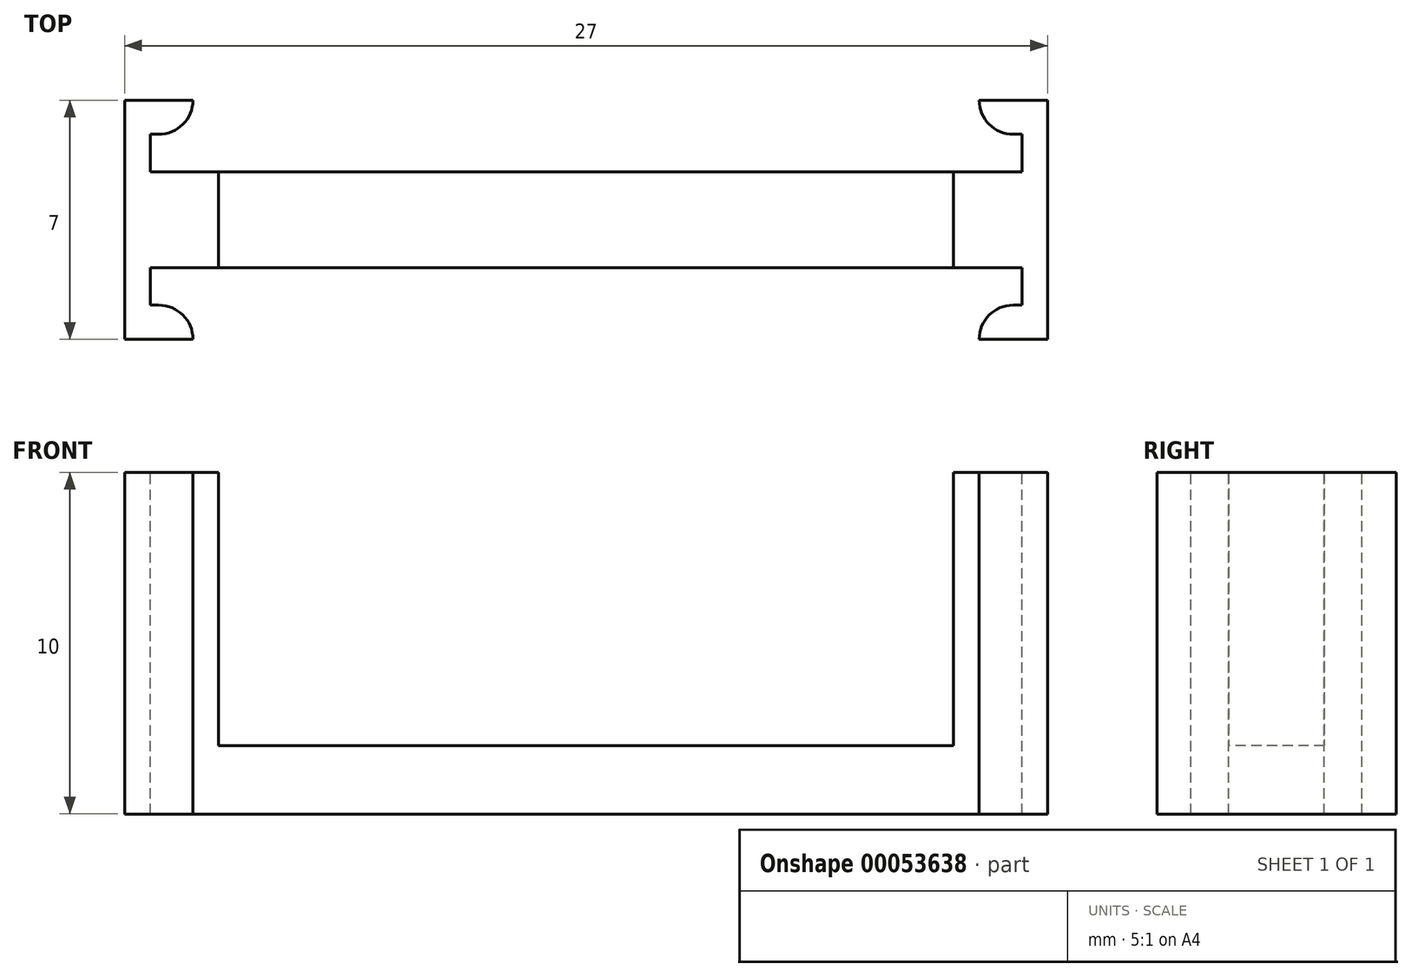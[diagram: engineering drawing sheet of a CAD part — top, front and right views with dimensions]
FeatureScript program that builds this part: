
annotation { "Feature Type Name" : "Feature", "Feature Type Description" : "" }
export const myFeature = defineFeature(function(context is Context, id is Id, definition is map)
    precondition{}
    {
        {
            var Q0;
            Q0=qCreatedBy(makeId("Front.planeOp"),FACE);
            var sketch = newSketch(context, id + "F0", { "sketchPlane" : qUnion([Q0])});
            skArc(sketch, "E0", {"start": v(0, 4.09) * mm, "mid": v(0.48, 4.1) * mm, "end": v(0.97, 4.15) * mm});
            skLineSegment(sketch, "E1", {"start": v(3.5, 7.49) * mm, "end": v(10.06, -2.83) * mm});
            skLineSegment(sketch, "E2", {"start": v(10.06, -2.83) * mm, "end": v(10.06, -5.91) * mm});
            skLineSegment(sketch, "E3", {"start": v(10.06, -5.91) * mm, "end": v(7.8, -5.91) * mm});
            skArc(sketch, "E4", {"start": v(7.8, -5.91) * mm, "mid": v(6.65, 0.66) * mm, "end": v(0.97, 4.15) * mm});
            skPoint(sketch, "E5.orphan", {"position": v(0, -5.91) * mm});
            skLineSegment(sketch, "E6", {"start": v(0, 4.09) * mm, "end": v(0, -5.91) * mm, "construction": true});
            skLineSegment(sketch, "E7", {"start": v(0, 4.09) * mm, "end": v(0, 7.49) * mm});
            skLineSegment(sketch, "E8", {"start": v(0, 7.49) * mm, "end": v(0, 9.49) * mm});
            skLineSegment(sketch, "E9", {"start": v(0, 9.49) * mm, "end": v(3.5, 9.49) * mm});
            skLineSegment(sketch, "E10", {"start": v(3.5, 9.49) * mm, "end": v(3.5, 7.49) * mm});
            skSolve(sketch);
        }
        {
            var Q0;
            Q0=qSketchRegion(id+"F0",true);
            var Q1;
            Q1=sQuery(id+"F0.wireOp",EDGE,"E6");
            revolve(context, id + "F1", {"entities" : qUnion([Q0]), "axis" : qUnion([Q1]), "revolveType" : RevolveType.FULL});
        }
        {
            var Q0;
            Q0=qCreatedBy(makeId("Top.planeOp"),FACE);
            var sketch = newSketch(context, id + "F2", { "sketchPlane" : qUnion([Q0])});
            skCircle(sketch, "E11", {"center": v(0, 0) * mm, "radius": 3 * mm});
            skSolve(sketch);
        }
        {
            var Q0;
            Q0=qSketchRegion(id+"F2",true);
            extrude(context, id + "F3", {"entities" : qUnion([Q0]), "operationType" : NewBodyOperationType.REMOVE, "endBound" : BoundingType.SYMMETRIC, "oppositeDirection" : true, "depth" : 50 * mm});
        }
        {
            var Q0;
            Q0=qCreatedBy(makeId("Right.planeOp"),FACE);
            var sketch = newSketch(context, id + "F4", { "sketchPlane" : qUnion([Q0])});
            skLineSegment(sketch, "E12.bottom", {"start": v(1, -5.91) * mm, "end": v(-1, -5.91) * mm});
            skLineSegment(sketch, "E12.left", {"start": v(1, -5.91) * mm, "end": v(1, -0.91) * mm});
            skLineSegment(sketch, "E12.right", {"start": v(-1, -5.91) * mm, "end": v(-1, -0.91) * mm});
            skArc(sketch, "E13", {"start": v(1, -0.91) * mm, "mid": v(0, 0.09) * mm, "end": v(-1, -0.91) * mm});
            skSolve(sketch);
        }
        {
            var Q0;
            Q0=qSketchRegion(id+"F4",true);
            extrude(context, id + "F5", {"entities" : qUnion([Q0]), "operationType" : NewBodyOperationType.REMOVE, "endBound" : BoundingType.SYMMETRIC, "oppositeDirection" : true, "depth" : 25 * mm});
        }
        {
            var Q0;
            Q0=makeQuery(id+"F1.opRevolve","SWEPT_EDGE",EDGE,{"disambiguationData":[OSD([sQuery(id+"F0.wireOp",EDGE,"E9"),sQuery(id+"F0.wireOp",EDGE,"E10")])]});
            fillet(context, id + "F6", {"entities" : qUnion([Q0]), "radius" : 1 * mm, "tangentPropagation" : true, "allowEdgeOverflow" : false});
        }
        {
            var Q0;
            {var subQ0=sQuery(id+"F0.wireOp",EDGE,"E2");var subQ1=sQuery(id+"F0.wireOp",EDGE,"E3");Q0=makeQuery(id+"F5.boolean.opBoolean","SPLIT",EDGE,{"disambiguationData":[TD([makeQuery(id+"F5.opExtrude","SWEPT_FACE",FACE,{"disambiguationData":[OSD([sQuery(id+"F4.wireOp",EDGE,"E12.right")])]})])],"derivedFrom":makeQuery(id+"F1.opRevolve","SWEPT_EDGE",EDGE,{"disambiguationData":[OSD([subQ0,subQ1])]})});}
            var Q1;
            {var subQ0=sQuery(id+"F0.wireOp",EDGE,"E2");var subQ1=sQuery(id+"F0.wireOp",EDGE,"E3");Q1=makeQuery(id+"F5.boolean.opBoolean","SPLIT",EDGE,{"disambiguationData":[TD([makeQuery(id+"F5.opExtrude","SWEPT_FACE",FACE,{"disambiguationData":[OSD([sQuery(id+"F4.wireOp",EDGE,"E12.left")])]})])],"derivedFrom":makeQuery(id+"F1.opRevolve","SWEPT_EDGE",EDGE,{"disambiguationData":[OSD([subQ0,subQ1])]})});}
            fillet(context, id + "F7", {"entities" : qUnion([Q0, Q1]), "radius" : 1 * mm, "tangentPropagation" : true, "allowEdgeOverflow" : false});
        }
        {
            var Q0;
            Q0=qCreatedBy(makeId("Front.planeOp"),FACE);
            var sketch = newSketch(context, id + "F8", { "sketchPlane" : qUnion([Q0])});
            skLineSegment(sketch, "E14.bottom", {"start": v(-13.5, 17.49) * mm, "end": v(13.5, 17.49) * mm});
            skLineSegment(sketch, "E14.top", {"start": v(-13.5, 7.49) * mm, "end": v(13.5, 7.49) * mm});
            skLineSegment(sketch, "E14.left", {"start": v(-13.5, 17.49) * mm, "end": v(-13.5, 7.49) * mm});
            skLineSegment(sketch, "E14.right", {"start": v(13.5, 17.49) * mm, "end": v(13.5, 7.49) * mm});
            skSolve(sketch);
        }
        {
            var Q0;
            Q0=qSketchRegion(id+"F8",true);
            extrude(context, id + "F9", {"entities" : qUnion([Q0]), "operationType" : NewBodyOperationType.ADD, "endBound" : BoundingType.SYMMETRIC, "depth" : 7 * mm, "offsetDistance" : 25 * mm});
        }
        {
            var Q0;
            Q0=makeQuery(id+"F9.opExtrude","SWEPT_FACE",FACE,{"disambiguationData":[OSD([sQuery(id+"F8.wireOp",EDGE,"E14.bottom")])]});
            var sketch = newSketch(context, id + "F10", { "sketchPlane" : qUnion([Q0])});
            skLineSegment(sketch, "E15.bottom", {"start": v(-12.75, 2.5) * mm, "end": v(-11.5, 2.5) * mm});
            skLineSegment(sketch, "E15.top", {"start": v(-12.75, 1.4) * mm, "end": v(12.75, 1.4) * mm});
            skLineSegment(sketch, "E15.left", {"start": v(-12.75, 2.5) * mm, "end": v(-12.75, 1.4) * mm});
            skLineSegment(sketch, "E15.right", {"start": v(12.75, 2.5) * mm, "end": v(12.75, 1.4) * mm});
            skLineSegment(sketch, "E16", {"start": v(-11.5, 2.5) * mm, "end": v(-11.5, 3.5) * mm});
            skLineSegment(sketch, "E17", {"start": v(-11.5, 3.5) * mm, "end": v(11.5, 3.5) * mm});
            skLineSegment(sketch, "E18", {"start": v(11.5, 3.5) * mm, "end": v(11.5, 2.5) * mm});
            skLineSegment(sketch, "E19.trimOffspring", {"start": v(11.5, 2.5) * mm, "end": v(12.75, 2.5) * mm});
            skLineSegment(sketch, "E20.MirrorCS", {"start": v(-11.5, -3.5) * mm, "end": v(11.5, -3.5) * mm});
            skLineSegment(sketch, "E21.MirrorCS", {"start": v(-12.75, -1.4) * mm, "end": v(12.75, -1.4) * mm});
            skLineSegment(sketch, "E22.MirrorCS", {"start": v(12.75, -2.5) * mm, "end": v(12.75, -1.4) * mm});
            skLineSegment(sketch, "E23.MirrorCS", {"start": v(11.5, -2.5) * mm, "end": v(12.75, -2.5) * mm});
            skLineSegment(sketch, "E24.MirrorCS", {"start": v(11.5, -3.5) * mm, "end": v(11.5, -2.5) * mm});
            skLineSegment(sketch, "E25.MirrorCS", {"start": v(-11.5, -2.5) * mm, "end": v(-11.5, -3.5) * mm});
            skLineSegment(sketch, "E26.MirrorCS", {"start": v(-12.75, -2.5) * mm, "end": v(-11.5, -2.5) * mm});
            skLineSegment(sketch, "E27.MirrorCS", {"start": v(-12.75, -2.5) * mm, "end": v(-12.75, -1.4) * mm});
            skSolve(sketch);
        }
        {
            var Q0;
            Q0=qSketchRegion(id+"F10",true);
            var Q1;
            {var subQ0=sQuery(id+"F8.wireOp",EDGE,"E14.right");var subQ2=sQuery(id+"F8.wireOp",EDGE,"E14.top");var subQ4=makeQuery(id+"F9.opExtrude","SWEPT_FACE",FACE,{"disambiguationData":[OSD([subQ2])]});Q1=makeQuery(id+"F9.boolean.opBoolean","SPLIT",FACE,{"disambiguationData":[TD([makeQuery(id+"F9.opExtrude","SWEPT_FACE",FACE,{"disambiguationData":[OSD([subQ0])]})])],"derivedFrom":subQ4});}
            extrude(context, id + "F11", {"entities" : qUnion([Q0]), "operationType" : NewBodyOperationType.REMOVE, "endBound" : BoundingType.UP_TO_SURFACE, "oppositeDirection" : true, "depth" : 25 * mm, "endBoundEntityFace" : qUnion([Q1]), "offsetDistance" : 25 * mm});
        }
        {
            var Q0;
            Q0=makeQuery(id+"F9.boolean.opBoolean","SPLIT",FACE,{"disambiguationData":[TD([makeQuery(id+"F3.boolean.opBoolean","COPY",FACE,{"derivedFrom":makeQuery(id+"F3.opExtrude","SWEPT_FACE",FACE,{"disambiguationData":[OSD([sQuery(id+"F2.wireOp",EDGE,"E11")])]})})])],"derivedFrom":makeQuery(id+"F9.opExtrude","SWEPT_FACE",FACE,{"disambiguationData":[OSD([sQuery(id+"F8.wireOp",EDGE,"E14.top")])]})});
            var sketch = newSketch(context, id + "F12", { "sketchPlane" : qUnion([Q0])});
            skCircle(sketch, "E28", {"center": v(0, 0) * mm, "radius": 3.07 * mm});
            skSolve(sketch);
        }
        {
            var Q0;
            Q0=qSketchRegion(id+"F12",true);
            extrude(context, id + "F13", {"entities" : qUnion([Q0]), "operationType" : NewBodyOperationType.ADD, "depth" : 2 * mm, "offsetDistance" : 25 * mm});
        }
        {
            var Q0;
            {var subQ0=sQuery(id+"F10.wireOp",EDGE,"E21.MirrorCS");var subQ1=makeQuery(id+"F11.opExtrude","SWEPT_FACE",FACE,{"disambiguationData":[OSD([subQ0])]});var subQ2=makeQuery(id+"F11.opExtrude","CAP_FACE",FACE,{"disambiguationData":[OSD([subQ0,sQuery(id+"F10.wireOp",EDGE,"E22.MirrorCS"),sQuery(id+"F10.wireOp",EDGE,"E23.MirrorCS"),sQuery(id+"F10.wireOp",EDGE,"E24.MirrorCS"),sQuery(id+"F10.wireOp",EDGE,"E25.MirrorCS"),sQuery(id+"F10.wireOp",EDGE,"E26.MirrorCS"),sQuery(id+"F10.wireOp",EDGE,"E27.MirrorCS"),sQuery(id+"F10.wireOp",EDGE,"E20.MirrorCS")])],"isStart":false});var subQ3=makeQuery(id+"F11.opExtrude","CAP_EDGE",EDGE,{"disambiguationData":[OSD([subQ0])],"isStart":false});var subQ4=makeQuery(id+"F9.opExtrude","SWEPT_FACE",FACE,{"disambiguationData":[OSD([sQuery(id+"F8.wireOp",EDGE,"E14.top")])]});Q0=makeQuery(id+"F13.boolean.opBoolean","MERGE",EDGE,{"derivedFrom":[makeQuery(id+"F11.boolean.opBoolean","COPY",EDGE,{"disambiguationData":[topologyDisambiguationEdgeConnected([subQ4,subQ1]),TD([makeQuery(id+"F3.boolean.opBoolean","COPY",FACE,{"derivedFrom":makeQuery(id+"F3.opExtrude","SWEPT_FACE",FACE,{"disambiguationData":[OSD([sQuery(id+"F2.wireOp",EDGE,"E11")])]})})])],"derivedFrom":subQ3}),makeQuery(id+"F11.boolean.opBoolean","COPY",EDGE,{"disambiguationData":[topologyDisambiguationEdgeConnected([subQ1,subQ2]),OD(0.0)],"derivedFrom":subQ3}),makeQuery(id+"F11.boolean.opBoolean","COPY",EDGE,{"disambiguationData":[topologyDisambiguationEdgeConnected([subQ1,subQ2]),OD(1.0)],"derivedFrom":subQ3})]});}
            var Q1;
            {var subQ0=sQuery(id+"F10.wireOp",EDGE,"E15.top");var subQ1=makeQuery(id+"F11.opExtrude","CAP_FACE",FACE,{"disambiguationData":[OSD([sQuery(id+"F10.wireOp",EDGE,"E15.bottom"),subQ0,sQuery(id+"F10.wireOp",EDGE,"E15.left"),sQuery(id+"F10.wireOp",EDGE,"E15.right"),sQuery(id+"F10.wireOp",EDGE,"E16"),sQuery(id+"F10.wireOp",EDGE,"E17"),sQuery(id+"F10.wireOp",EDGE,"E18"),sQuery(id+"F10.wireOp",EDGE,"E19.trimOffspring")])],"isStart":false});var subQ2=makeQuery(id+"F11.opExtrude","SWEPT_FACE",FACE,{"disambiguationData":[OSD([subQ0])]});var subQ3=makeQuery(id+"F11.opExtrude","CAP_EDGE",EDGE,{"disambiguationData":[OSD([subQ0])],"isStart":false});var subQ4=makeQuery(id+"F9.opExtrude","SWEPT_FACE",FACE,{"disambiguationData":[OSD([sQuery(id+"F8.wireOp",EDGE,"E14.top")])]});Q1=makeQuery(id+"F13.boolean.opBoolean","MERGE",EDGE,{"derivedFrom":[makeQuery(id+"F11.boolean.opBoolean","COPY",EDGE,{"disambiguationData":[topologyDisambiguationEdgeConnected([subQ4,subQ2]),TD([makeQuery(id+"F3.boolean.opBoolean","COPY",FACE,{"derivedFrom":makeQuery(id+"F3.opExtrude","SWEPT_FACE",FACE,{"disambiguationData":[OSD([sQuery(id+"F2.wireOp",EDGE,"E11")])]})})])],"derivedFrom":subQ3}),makeQuery(id+"F11.boolean.opBoolean","COPY",EDGE,{"disambiguationData":[topologyDisambiguationEdgeConnected([subQ1,subQ2]),OD(0.0)],"derivedFrom":subQ3}),makeQuery(id+"F11.boolean.opBoolean","COPY",EDGE,{"disambiguationData":[topologyDisambiguationEdgeConnected([subQ1,subQ2]),OD(1.0)],"derivedFrom":subQ3})]});}
            var Q2;
            Q2=makeQuery(id+"F11.boolean.opBoolean","COPY",EDGE,{"derivedFrom":makeQuery(id+"F11.opExtrude","SWEPT_EDGE",EDGE,{"disambiguationData":[OSD([sQuery(id+"F10.wireOp",EDGE,"E23.MirrorCS"),sQuery(id+"F10.wireOp",EDGE,"E24.MirrorCS")])]})});
            var Q3;
            Q3=makeQuery(id+"F11.boolean.opBoolean","COPY",EDGE,{"derivedFrom":makeQuery(id+"F11.opExtrude","SWEPT_EDGE",EDGE,{"disambiguationData":[OSD([sQuery(id+"F10.wireOp",EDGE,"E18"),sQuery(id+"F10.wireOp",EDGE,"E19.trimOffspring")])]})});
            var Q4;
            Q4=makeQuery(id+"F11.boolean.opBoolean","COPY",EDGE,{"derivedFrom":makeQuery(id+"F11.opExtrude","SWEPT_EDGE",EDGE,{"disambiguationData":[OSD([sQuery(id+"F10.wireOp",EDGE,"E15.bottom"),sQuery(id+"F10.wireOp",EDGE,"E16")])]})});
            var Q5;
            Q5=makeQuery(id+"F11.boolean.opBoolean","COPY",EDGE,{"derivedFrom":makeQuery(id+"F11.opExtrude","SWEPT_EDGE",EDGE,{"disambiguationData":[OSD([sQuery(id+"F10.wireOp",EDGE,"E25.MirrorCS"),sQuery(id+"F10.wireOp",EDGE,"E26.MirrorCS")])]})});
            fillet(context, id + "F14", {"entities" : qUnion([Q0, Q1, Q2, Q3, Q4, Q5]), "radius" : 1 * mm, "tangentPropagation" : true, "allowEdgeOverflow" : false});
        }
        {
            var Q0;
            Q0=makeQuery(id+"F11.boolean.opBoolean","SPLIT",EDGE,{"derivedFrom":makeQuery(id+"F9.boolean.opBoolean","SPLIT",EDGE,{"disambiguationData":[OD(0.0)],"derivedFrom":makeQuery(id+"F1.opRevolve","SWEPT_EDGE",EDGE,{"disambiguationData":[OSD([sQuery(id+"F0.wireOp",EDGE,"E1"),sQuery(id+"F0.wireOp",EDGE,"E10")])]})})});
            var Q1;
            Q1=makeQuery(id+"F11.boolean.opBoolean","SPLIT",EDGE,{"derivedFrom":makeQuery(id+"F9.boolean.opBoolean","SPLIT",EDGE,{"disambiguationData":[OD(1.0)],"derivedFrom":makeQuery(id+"F1.opRevolve","SWEPT_EDGE",EDGE,{"disambiguationData":[OSD([sQuery(id+"F0.wireOp",EDGE,"E1"),sQuery(id+"F0.wireOp",EDGE,"E10")])]})})});
            var Q2;
            {var subQ0=sQuery(id+"F10.wireOp",EDGE,"E21.MirrorCS");var subQ2=sQuery(id+"F8.wireOp",EDGE,"E14.left");var subQ3=sQuery(id+"F8.wireOp",EDGE,"E14.top");var subQ5=makeQuery(id+"F9.opExtrude","SWEPT_FACE",FACE,{"disambiguationData":[OSD([subQ3])]});var subQ6=makeQuery(id+"F1.opRevolve","SWEPT_FACE",FACE,{"disambiguationData":[OSD([sQuery(id+"F0.wireOp",EDGE,"E1")])]});Q2=makeQuery(id+"F14.opFillet","TWEAK_EDGE",EDGE,{"derivedFrom":[makeQuery(id+"F11.boolean.opBoolean","TWEAK_VERTEX",VERTEX,{"derivedFrom":[subQ6,makeQuery(id+"F9.boolean.opBoolean","SPLIT",FACE,{"disambiguationData":[TD([makeQuery(id+"F9.opExtrude","SWEPT_FACE",FACE,{"disambiguationData":[OSD([subQ2])]})])],"derivedFrom":subQ5}),makeQuery(id+"F11.opExtrude","SWEPT_FACE",FACE,{"disambiguationData":[OSD([subQ0])]}),makeQuery(id+"F11.opExtrude","CAP_FACE",FACE,{"disambiguationData":[OSD([subQ0,sQuery(id+"F10.wireOp",EDGE,"E22.MirrorCS"),sQuery(id+"F10.wireOp",EDGE,"E23.MirrorCS"),sQuery(id+"F10.wireOp",EDGE,"E24.MirrorCS"),sQuery(id+"F10.wireOp",EDGE,"E25.MirrorCS"),sQuery(id+"F10.wireOp",EDGE,"E26.MirrorCS"),sQuery(id+"F10.wireOp",EDGE,"E27.MirrorCS"),sQuery(id+"F10.wireOp",EDGE,"E20.MirrorCS")])],"isStart":false})]})]});}
            var Q3;
            {var subQ0=sQuery(id+"F10.wireOp",EDGE,"E21.MirrorCS");var subQ1=sQuery(id+"F8.wireOp",EDGE,"E14.right");var subQ3=sQuery(id+"F8.wireOp",EDGE,"E14.top");var subQ5=makeQuery(id+"F9.opExtrude","SWEPT_FACE",FACE,{"disambiguationData":[OSD([subQ3])]});var subQ6=makeQuery(id+"F1.opRevolve","SWEPT_FACE",FACE,{"disambiguationData":[OSD([sQuery(id+"F0.wireOp",EDGE,"E1")])]});Q3=makeQuery(id+"F14.opFillet","TWEAK_EDGE",EDGE,{"derivedFrom":[makeQuery(id+"F11.boolean.opBoolean","TWEAK_VERTEX",VERTEX,{"derivedFrom":[subQ6,makeQuery(id+"F9.boolean.opBoolean","SPLIT",FACE,{"disambiguationData":[TD([makeQuery(id+"F9.opExtrude","SWEPT_FACE",FACE,{"disambiguationData":[OSD([subQ1])]})])],"derivedFrom":subQ5}),makeQuery(id+"F11.opExtrude","SWEPT_FACE",FACE,{"disambiguationData":[OSD([subQ0])]}),makeQuery(id+"F11.opExtrude","CAP_FACE",FACE,{"disambiguationData":[OSD([subQ0,sQuery(id+"F10.wireOp",EDGE,"E22.MirrorCS"),sQuery(id+"F10.wireOp",EDGE,"E23.MirrorCS"),sQuery(id+"F10.wireOp",EDGE,"E24.MirrorCS"),sQuery(id+"F10.wireOp",EDGE,"E25.MirrorCS"),sQuery(id+"F10.wireOp",EDGE,"E26.MirrorCS"),sQuery(id+"F10.wireOp",EDGE,"E27.MirrorCS"),sQuery(id+"F10.wireOp",EDGE,"E20.MirrorCS")])],"isStart":false})]})]});}
            var Q4;
            {var subQ0=sQuery(id+"F10.wireOp",EDGE,"E15.top");var subQ1=sQuery(id+"F8.wireOp",EDGE,"E14.right");var subQ3=sQuery(id+"F8.wireOp",EDGE,"E14.top");var subQ5=makeQuery(id+"F9.opExtrude","SWEPT_FACE",FACE,{"disambiguationData":[OSD([subQ3])]});var subQ6=makeQuery(id+"F1.opRevolve","SWEPT_FACE",FACE,{"disambiguationData":[OSD([sQuery(id+"F0.wireOp",EDGE,"E1")])]});Q4=makeQuery(id+"F14.opFillet","TWEAK_EDGE",EDGE,{"derivedFrom":[makeQuery(id+"F11.boolean.opBoolean","TWEAK_VERTEX",VERTEX,{"derivedFrom":[subQ6,makeQuery(id+"F9.boolean.opBoolean","SPLIT",FACE,{"disambiguationData":[TD([makeQuery(id+"F9.opExtrude","SWEPT_FACE",FACE,{"disambiguationData":[OSD([subQ1])]})])],"derivedFrom":subQ5}),makeQuery(id+"F11.opExtrude","CAP_FACE",FACE,{"disambiguationData":[OSD([sQuery(id+"F10.wireOp",EDGE,"E15.bottom"),subQ0,sQuery(id+"F10.wireOp",EDGE,"E15.left"),sQuery(id+"F10.wireOp",EDGE,"E15.right"),sQuery(id+"F10.wireOp",EDGE,"E16"),sQuery(id+"F10.wireOp",EDGE,"E17"),sQuery(id+"F10.wireOp",EDGE,"E18"),sQuery(id+"F10.wireOp",EDGE,"E19.trimOffspring")])],"isStart":false}),makeQuery(id+"F11.opExtrude","SWEPT_FACE",FACE,{"disambiguationData":[OSD([subQ0])]})]})]});}
            var Q5;
            {var subQ0=sQuery(id+"F10.wireOp",EDGE,"E15.top");var subQ2=sQuery(id+"F8.wireOp",EDGE,"E14.left");var subQ3=sQuery(id+"F8.wireOp",EDGE,"E14.top");var subQ5=makeQuery(id+"F9.opExtrude","SWEPT_FACE",FACE,{"disambiguationData":[OSD([subQ3])]});var subQ6=makeQuery(id+"F1.opRevolve","SWEPT_FACE",FACE,{"disambiguationData":[OSD([sQuery(id+"F0.wireOp",EDGE,"E1")])]});Q5=makeQuery(id+"F14.opFillet","TWEAK_EDGE",EDGE,{"derivedFrom":[makeQuery(id+"F11.boolean.opBoolean","TWEAK_VERTEX",VERTEX,{"derivedFrom":[subQ6,makeQuery(id+"F9.boolean.opBoolean","SPLIT",FACE,{"disambiguationData":[TD([makeQuery(id+"F9.opExtrude","SWEPT_FACE",FACE,{"disambiguationData":[OSD([subQ2])]})])],"derivedFrom":subQ5}),makeQuery(id+"F11.opExtrude","CAP_FACE",FACE,{"disambiguationData":[OSD([sQuery(id+"F10.wireOp",EDGE,"E15.bottom"),subQ0,sQuery(id+"F10.wireOp",EDGE,"E15.left"),sQuery(id+"F10.wireOp",EDGE,"E15.right"),sQuery(id+"F10.wireOp",EDGE,"E16"),sQuery(id+"F10.wireOp",EDGE,"E17"),sQuery(id+"F10.wireOp",EDGE,"E18"),sQuery(id+"F10.wireOp",EDGE,"E19.trimOffspring")])],"isStart":false}),makeQuery(id+"F11.opExtrude","SWEPT_FACE",FACE,{"disambiguationData":[OSD([subQ0])]})]})]});}
            var Q6;
            Q6=makeQuery(id+"F11.boolean.opBoolean","COPY",EDGE,{"derivedFrom":makeQuery(id+"F11.opExtrude","CAP_EDGE",EDGE,{"disambiguationData":[OSD([sQuery(id+"F10.wireOp",EDGE,"E15.top")])],"isStart":true})});
            var Q7;
            Q7=makeQuery(id+"F11.boolean.opBoolean","COPY",EDGE,{"derivedFrom":makeQuery(id+"F11.opExtrude","CAP_EDGE",EDGE,{"disambiguationData":[OSD([sQuery(id+"F10.wireOp",EDGE,"E15.left")])],"isStart":true})});
            var Q8;
            Q8=makeQuery(id+"F11.boolean.opBoolean","COPY",EDGE,{"derivedFrom":makeQuery(id+"F11.opExtrude","CAP_EDGE",EDGE,{"disambiguationData":[OSD([sQuery(id+"F10.wireOp",EDGE,"E15.bottom")])],"isStart":true})});
            var Q9;
            Q9=makeQuery(id+"F11.boolean.opBoolean","COPY",EDGE,{"derivedFrom":makeQuery(id+"F11.opExtrude","CAP_EDGE",EDGE,{"disambiguationData":[OSD([sQuery(id+"F10.wireOp",EDGE,"E21.MirrorCS")])],"isStart":true})});
            var Q10;
            Q10=makeQuery(id+"F11.boolean.opBoolean","COPY",EDGE,{"derivedFrom":makeQuery(id+"F11.opExtrude","CAP_EDGE",EDGE,{"disambiguationData":[OSD([sQuery(id+"F10.wireOp",EDGE,"E27.MirrorCS")])],"isStart":true})});
            var Q11;
            Q11=makeQuery(id+"F11.boolean.opBoolean","COPY",EDGE,{"derivedFrom":makeQuery(id+"F11.opExtrude","CAP_EDGE",EDGE,{"disambiguationData":[OSD([sQuery(id+"F10.wireOp",EDGE,"E26.MirrorCS")])],"isStart":true})});
            var Q12;
            Q12=makeQuery(id+"F11.boolean.opBoolean","COPY",EDGE,{"derivedFrom":makeQuery(id+"F11.opExtrude","CAP_EDGE",EDGE,{"disambiguationData":[OSD([sQuery(id+"F10.wireOp",EDGE,"E22.MirrorCS")])],"isStart":true})});
            var Q13;
            Q13=makeQuery(id+"F11.boolean.opBoolean","COPY",EDGE,{"derivedFrom":makeQuery(id+"F11.opExtrude","CAP_EDGE",EDGE,{"disambiguationData":[OSD([sQuery(id+"F10.wireOp",EDGE,"E23.MirrorCS")])],"isStart":true})});
            var Q14;
            Q14=makeQuery(id+"F11.boolean.opBoolean","COPY",EDGE,{"derivedFrom":makeQuery(id+"F11.opExtrude","CAP_EDGE",EDGE,{"disambiguationData":[OSD([sQuery(id+"F10.wireOp",EDGE,"E15.right")])],"isStart":true})});
            var Q15;
            Q15=makeQuery(id+"F11.boolean.opBoolean","COPY",EDGE,{"derivedFrom":makeQuery(id+"F11.opExtrude","CAP_EDGE",EDGE,{"disambiguationData":[OSD([sQuery(id+"F10.wireOp",EDGE,"E19.trimOffspring")])],"isStart":true})});
            fillet(context, id + "F15", {"entities" : qUnion([Q0, Q1, Q2, Q3, Q4, Q5, Q6, Q7, Q8, Q9, Q10, Q11, Q12, Q13, Q14, Q15]), "radius" : 1 * mm, "tangentPropagation" : true, "allowEdgeOverflow" : false});
        }
        {
            var Q0;
            Q0=makeQuery(id+"F9.opExtrude","SWEPT_FACE",FACE,{"disambiguationData":[OSD([sQuery(id+"F8.wireOp",EDGE,"E14.bottom")])]});
            var sketch = newSketch(context, id + "F16", { "sketchPlane" : qUnion([Q0])});
            skLineSegment(sketch, "E29.bottom", {"start": v(-10.75, 2.5) * mm, "end": v(10.75, 2.5) * mm});
            skLineSegment(sketch, "E29.top", {"start": v(-10.75, -2.81) * mm, "end": v(10.75, -2.81) * mm});
            skLineSegment(sketch, "E29.left", {"start": v(-10.75, 2.5) * mm, "end": v(-10.75, -2.81) * mm});
            skLineSegment(sketch, "E29.right", {"start": v(10.75, 2.5) * mm, "end": v(10.75, -2.81) * mm});
            skSolve(sketch);
        }
        {
            var Q0;
            Q0=qSketchRegion(id+"F16",true);
            extrude(context, id + "F17", {"entities" : qUnion([Q0]), "operationType" : NewBodyOperationType.REMOVE, "oppositeDirection" : true, "depth" : 8 * mm, "offsetDistance" : 25 * mm});
        }
        {
            var Q0;
            Q0=makeQuery(id+"F5.boolean.opBoolean","SPLIT",FACE,{"disambiguationData":[TD([makeQuery(id+"F5.opExtrude","SWEPT_FACE",FACE,{"disambiguationData":[OSD([sQuery(id+"F4.wireOp",EDGE,"E12.right")])]})])],"derivedFrom":makeQuery(id+"F1.opRevolve","SWEPT_FACE",FACE,{"disambiguationData":[OSD([sQuery(id+"F0.wireOp",EDGE,"E3")])]})});
            var sketch = newSketch(context, id + "F18", { "sketchPlane" : qUnion([Q0])});
            skCircle(sketch, "E30", {"center": v(0, 0) * mm, "radius": 18.04 * mm});
            skSolve(sketch);
        }
        {
            var Q0;
            Q0 = qSketchRegion(id + "F18", true);
            var Q1;
            {var subQ1=sQuery(id+"F8.wireOp",EDGE,"E14.left");var subQ2=sQuery(id+"F8.wireOp",EDGE,"E14.top");var subQ4=makeQuery(id+"F9.opExtrude","SWEPT_FACE",FACE,{"disambiguationData":[OSD([subQ2])]});Q1=makeQuery(id+"F9.boolean.opBoolean","SPLIT",FACE,{"disambiguationData":[TD([makeQuery(id+"F9.opExtrude","SWEPT_FACE",FACE,{"disambiguationData":[OSD([subQ1])]})])],"derivedFrom":subQ4});}
            extrude(context, id + "F19", {"entities" : qUnion([Q0]), "operationType" : NewBodyOperationType.REMOVE, "endBound" : BoundingType.UP_TO_SURFACE, "oppositeDirection" : true, "depth" : 25 * mm, "endBoundEntityFace" : qUnion([Q1]), "offsetDistance" : 25 * mm});
        }
        {
            var Q0;
            Q0=makeQuery(id+"F17.boolean.opBoolean","COPY",FACE,{"derivedFrom":makeQuery(id+"F17.opExtrude","CAP_FACE",FACE,{"disambiguationData":[OSD([sQuery(id+"F16.wireOp",EDGE,"E29.bottom"),sQuery(id+"F16.wireOp",EDGE,"E29.top"),sQuery(id+"F16.wireOp",EDGE,"E29.left"),sQuery(id+"F16.wireOp",EDGE,"E29.right")])],"isStart":false})});
            var sketch = newSketch(context, id + "F20", { "sketchPlane" : qUnion([Q0])});
            skLineSegment(sketch, "E31.bottom", {"start": v(-8.3, 7.48) * mm, "end": v(7.07, 7.48) * mm});
            skLineSegment(sketch, "E31.top", {"start": v(-8.3, 1.4) * mm, "end": v(7.07, 1.4) * mm});
            skLineSegment(sketch, "E31.left", {"start": v(-8.3, 7.48) * mm, "end": v(-8.3, 1.4) * mm});
            skLineSegment(sketch, "E31.right", {"start": v(7.07, 7.48) * mm, "end": v(7.07, 1.4) * mm});
            skLineSegment(sketch, "E32.bottom", {"start": v(-8.16, -1.4) * mm, "end": v(6.98, -1.4) * mm});
            skLineSegment(sketch, "E32.top", {"start": v(-8.16, -7.27) * mm, "end": v(6.98, -7.27) * mm});
            skLineSegment(sketch, "E32.left", {"start": v(-8.16, -1.4) * mm, "end": v(-8.16, -7.27) * mm});
            skLineSegment(sketch, "E32.right", {"start": v(6.98, -1.4) * mm, "end": v(6.98, -7.27) * mm});
            skSolve(sketch);
        }
        {
            var Q0;
            Q0 = qSketchRegion(id + "F20", true);
            extrude(context, id + "F21", {"entities" : qUnion([Q0]), "operationType" : NewBodyOperationType.REMOVE, "oppositeDirection" : true, "depth" : 25 * mm, "offsetDistance" : 25 * mm});
        }
    });
